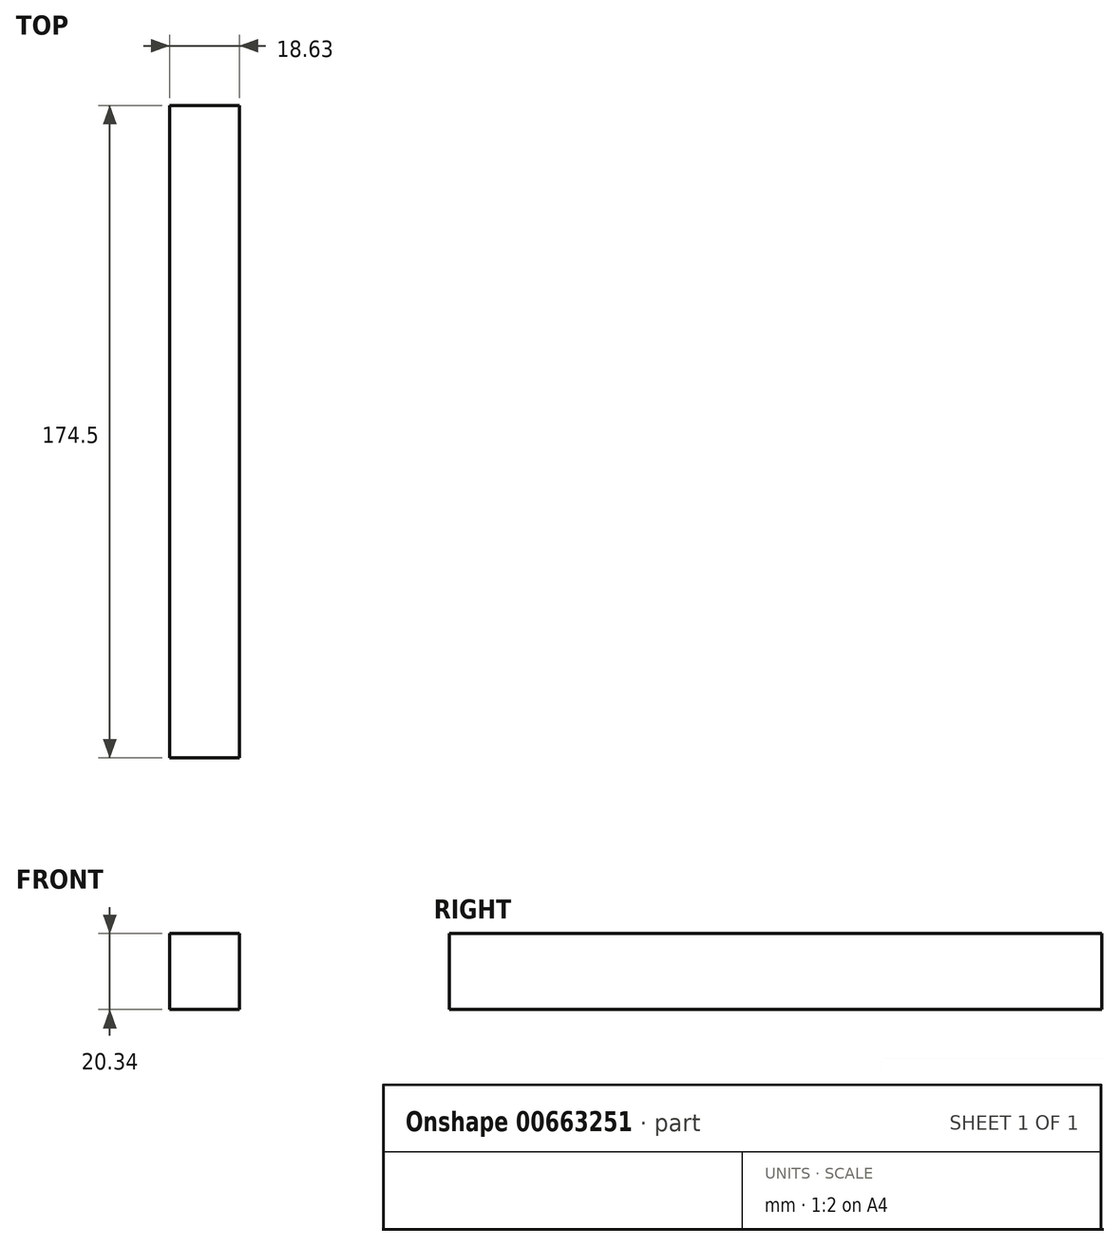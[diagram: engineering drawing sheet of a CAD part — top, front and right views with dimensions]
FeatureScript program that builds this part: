
annotation { "Feature Type Name" : "Feature", "Feature Type Description" : "" }
export const myFeature = defineFeature(function(context is Context, id is Id, definition is map)
    precondition{}
    {
        {
            var Q0;
            Q0=qCreatedBy(makeId("Front.planeOp"),FACE);
            var sketch = newSketch(context, id + "F0", { "sketchPlane" : qUnion([Q0])});
            skLineSegment(sketch, "E0.bottom", {"start": v(-40.56, 38.47) * mm, "end": v(-21.93, 38.47) * mm});
            skLineSegment(sketch, "E0.top", {"start": v(-40.56, 18.13) * mm, "end": v(-21.93, 18.13) * mm});
            skLineSegment(sketch, "E0.left", {"start": v(-40.56, 38.47) * mm, "end": v(-40.56, 18.13) * mm});
            skLineSegment(sketch, "E0.right", {"start": v(-21.93, 38.47) * mm, "end": v(-21.93, 18.13) * mm});
            skSolve(sketch);
        }
        {
            var Q0;
            Q0=makeQuery(id+"F0.imprint","IMPRINT",FACE,{"disambiguationData":[TD([[makeQuery(id+"F0.imprint","IMPRINT",EDGE,{"derivedFrom":sQuery(id+"F0.wireOp",EDGE,"E0.bottom")}),-1.0]])]});
            extrude(context, id + "F1", {"entities" : qUnion([Q0]), "depth" : 174.5 * mm, "offsetDistance" : 25.4 * mm});
        }
    });
